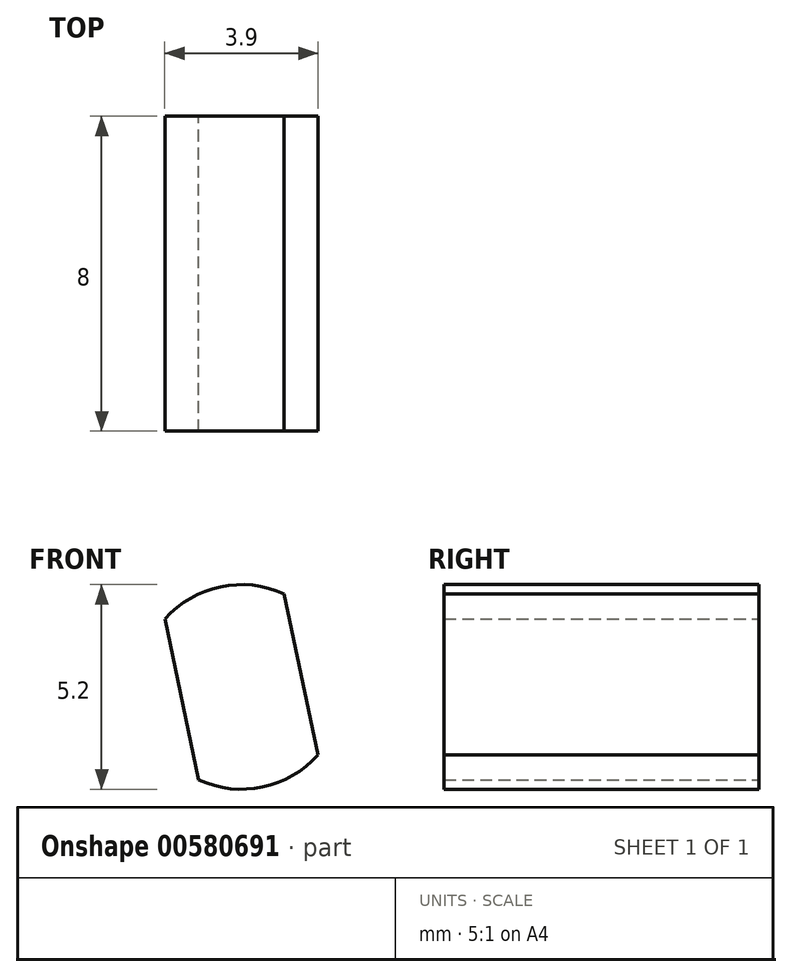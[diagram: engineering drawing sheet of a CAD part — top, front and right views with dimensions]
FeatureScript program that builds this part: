
annotation { "Feature Type Name" : "Feature", "Feature Type Description" : "" }
export const myFeature = defineFeature(function(context is Context, id is Id, definition is map)
    precondition{}
    {
        {
            var Q0;
            Q0=qCreatedBy(makeId("Front.planeOp"),FACE);
            var sketch = newSketch(context, id + "F0", { "sketchPlane" : qUnion([Q0])});
            skCircle(sketch, "E0", {"center": v(0, 0) * mm, "radius": 2.6 * mm});
            skLineSegment(sketch, "E1.left", {"start": v(1.95, -1.72) * mm, "end": v(1.09, 2.36) * mm});
            skLineSegment(sketch, "E1.right", {"start": v(-1.09, -2.36) * mm, "end": v(-1.95, 1.72) * mm});
            skSolve(sketch);
        }
        {
            var Q0;
            Q0=sQuery(id+"F0.wireOp",EDGE,"E0");
            extrude(context, id + "F1", {"bodyType" : ToolBodyType.SURFACE, "surfaceEntities" : qUnion([Q0]), "oppositeDirection" : true, "depth" : 5 * mm, "offsetDistance" : 25 * mm});
        }
        {
            var Q0;
            {var subQ0=sQuery(id+"F0.wireOp",EDGE,"E1.left");Q0=makeQuery(id+"F0.imprint","IMPRINT",FACE,{"disambiguationData":[TD([[makeQuery(id+"F0.imprint","IMPRINT",EDGE,{"derivedFrom":subQ0}),1.0]])]});}
            extrude(context, id + "F2", {"entities" : qUnion([Q0]), "depth" : 8 * mm, "offsetDistance" : 25 * mm});
        }
    });
